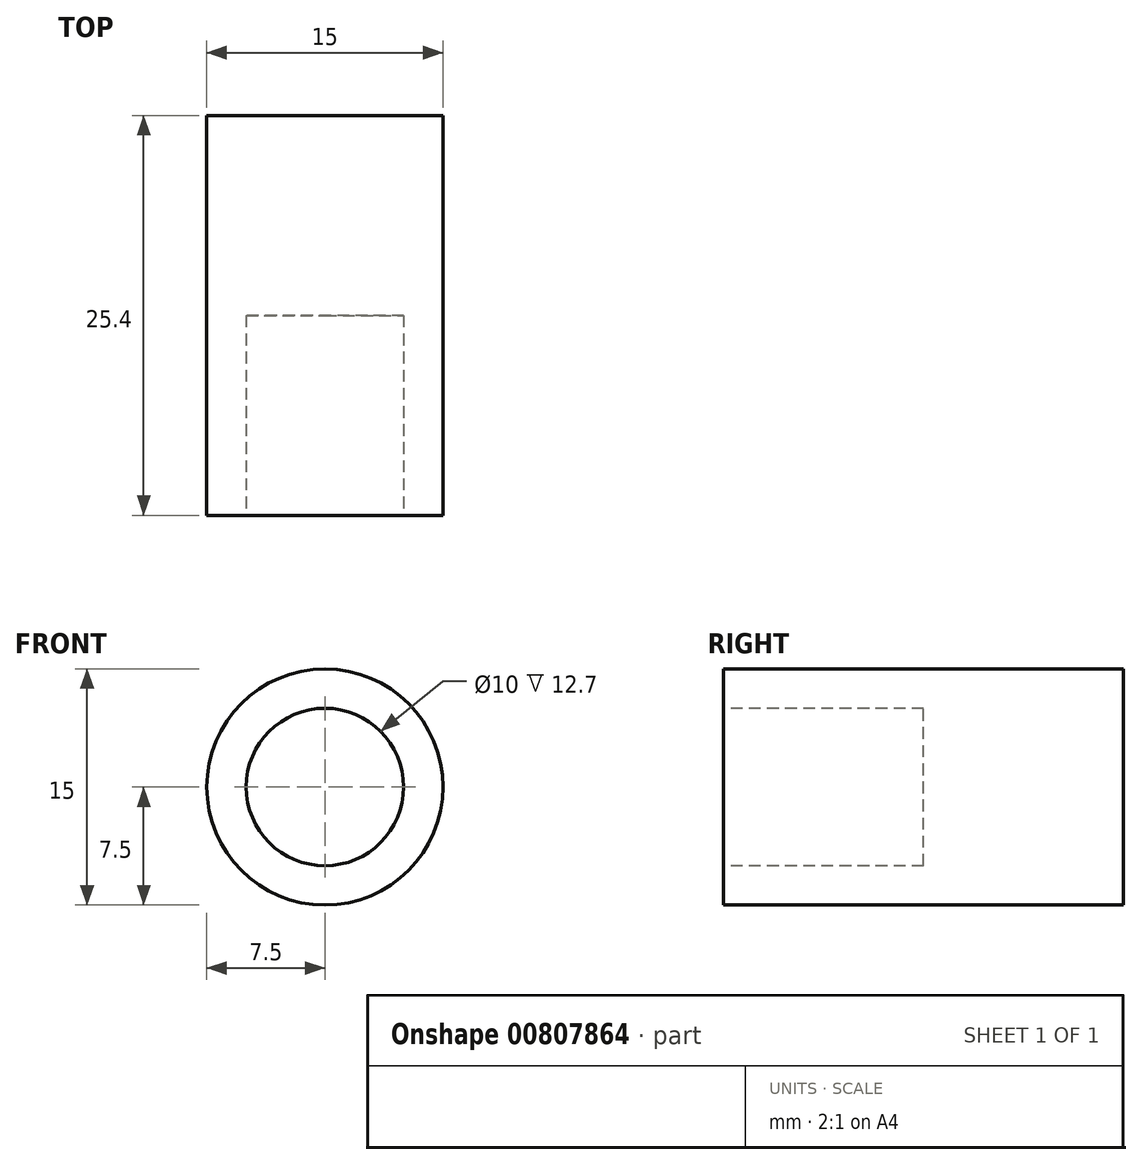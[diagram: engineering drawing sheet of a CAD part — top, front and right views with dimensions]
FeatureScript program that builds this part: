
annotation { "Feature Type Name" : "Feature", "Feature Type Description" : "" }
export const myFeature = defineFeature(function(context is Context, id is Id, definition is map)
    precondition{}
    {
        {
            var Q0;
            Q0=qCreatedBy(makeId("Right.planeOp"),FACE);
            var sketch = newSketch(context, id + "F0", { "sketchPlane" : qUnion([Q0])});
            skLineSegment(sketch, "E0.bottom", {"start": v(0, 7.5) * mm, "end": v(25.4, 7.5) * mm});
            skLineSegment(sketch, "E1.bottom", {"start": v(0, 5) * mm, "end": v(12.7, 5) * mm});
            skLineSegment(sketch, "E2", {"start": v(0, 0) * mm, "end": v(28.9, 0) * mm});
            skLineSegment(sketch, "E3", {"start": v(12.7, 5) * mm, "end": v(12.7, 0) * mm});
            skLineSegment(sketch, "E4", {"start": v(12.7, 0) * mm, "end": v(25.4, 0) * mm});
            skLineSegment(sketch, "E5", {"start": v(25.4, 0) * mm, "end": v(25.4, 7.5) * mm});
            skLineSegment(sketch, "E6", {"start": v(0, 7.5) * mm, "end": v(0, 5) * mm});
            skSolve(sketch);
        }
        {
            var Q0;
            Q0=makeQuery(id+"F0.imprint","IMPRINT",FACE,{"disambiguationData":[TD([[makeQuery(id+"F0.imprint","IMPRINT",EDGE,{"derivedFrom":sQuery(id+"F0.wireOp",EDGE,"E0.bottom")}),-1.0]])]});
            var Q1;
            Q1=sQuery(id+"F0.wireOp",EDGE,"E2");
            revolve(context, id + "F1", {"surfaceOperationType" : NewSurfaceOperationType.NEW, "entities" : qUnion([Q0]), "axis" : qUnion([Q1]), "revolveType" : RevolveType.FULL});
        }
    });
